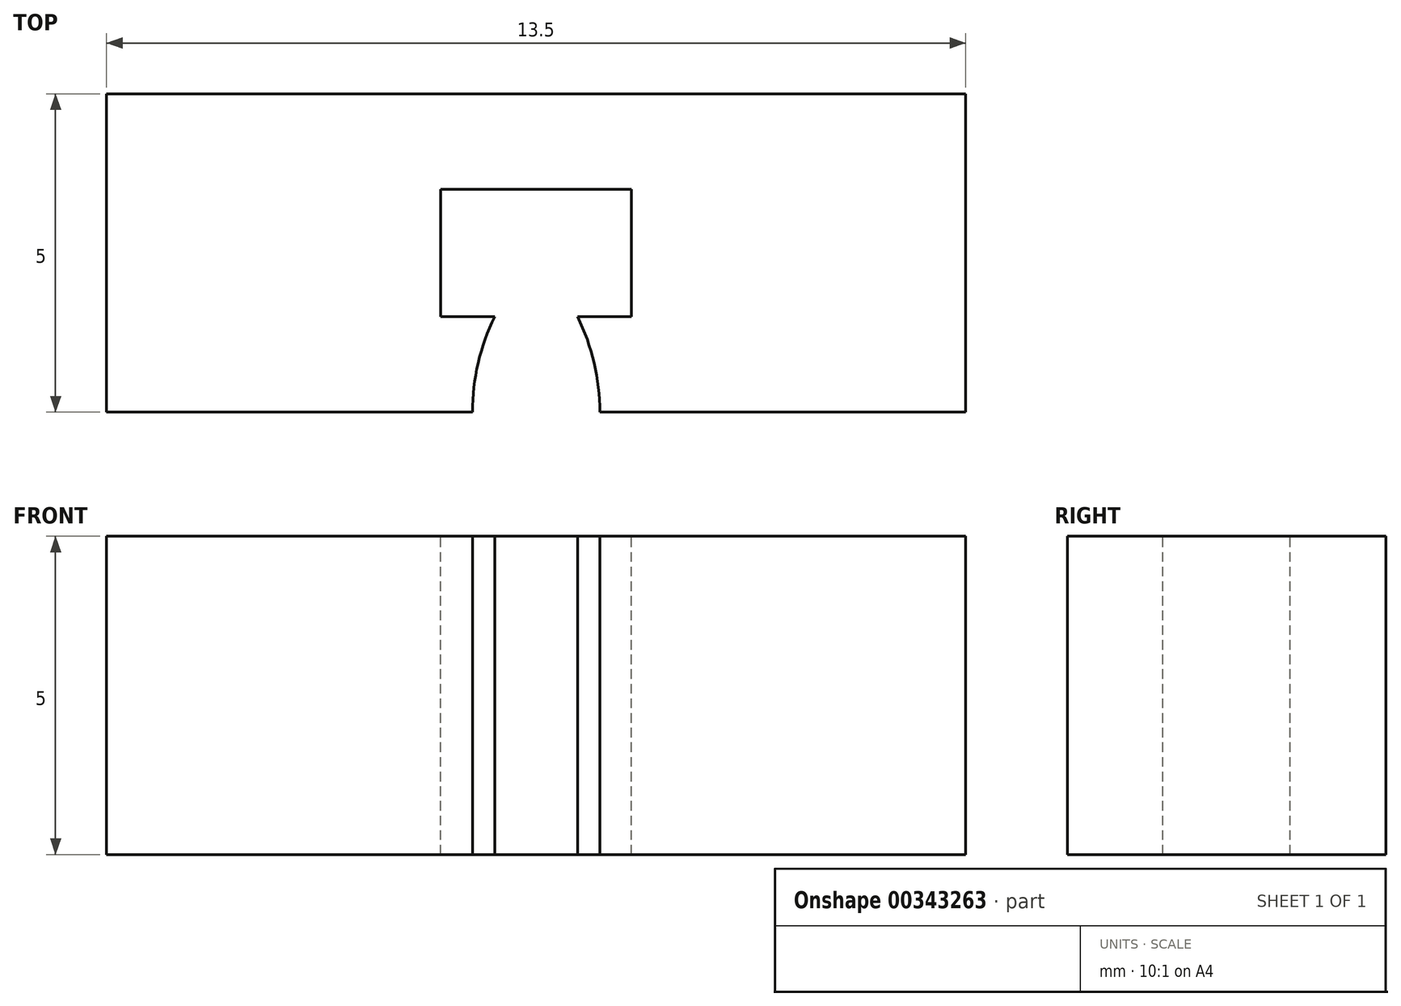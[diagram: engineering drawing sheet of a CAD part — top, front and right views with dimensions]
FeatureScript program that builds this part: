
annotation { "Feature Type Name" : "Feature", "Feature Type Description" : "" }
export const myFeature = defineFeature(function(context is Context, id is Id, definition is map)
    precondition{}
    {
        {
            var Q0;
            Q0=qCreatedBy(makeId("Top.planeOp"),FACE);
            var sketch = newSketch(context, id + "F0", { "sketchPlane" : qUnion([Q0])});
            skLineSegment(sketch, "E0.bottom", {"start": v(6.75, 2.5) * mm, "end": v(-6.75, 2.5) * mm});
            skLineSegment(sketch, "E0.top", {"start": v(6.75, -2.5) * mm, "end": v(-6.75, -2.5) * mm});
            skLineSegment(sketch, "E0.left", {"start": v(6.75, 2.5) * mm, "end": v(6.75, -2.5) * mm});
            skLineSegment(sketch, "E0.right", {"start": v(-6.75, 2.5) * mm, "end": v(-6.75, -2.5) * mm});
            skPoint(sketch, "E0.middle", {"position": v(0, 0) * mm});
            skSolve(sketch);
        }
        {
            var Q0;
            Q0=makeQuery(id+"F0.imprint","IMPRINT",FACE,{"disambiguationData":[TD([[makeQuery(id+"F0.imprint","IMPRINT",EDGE,{"derivedFrom":sQuery(id+"F0.wireOp",EDGE,"E0.bottom")}),1.0]])]});
            extrude(context, id + "F1", {"entities" : qUnion([Q0]), "depth" : 5 * mm});
        }
        {
            var Q0;
            Q0=makeQuery(id+"F1.opExtrude","CAP_FACE",FACE,{"disambiguationData":[OSD([sQuery(id+"F0.wireOp",EDGE,"E0.bottom"),sQuery(id+"F0.wireOp",EDGE,"E0.top"),sQuery(id+"F0.wireOp",EDGE,"E0.left"),sQuery(id+"F0.wireOp",EDGE,"E0.right")])],"isStart":false});
            var sketch = newSketch(context, id + "F2", { "sketchPlane" : qUnion([Q0])});
            skLineSegment(sketch, "E1.bottom", {"start": v(1.5, 1) * mm, "end": v(-1.5, 1) * mm});
            skLineSegment(sketch, "E1.top", {"start": v(1.5, -1) * mm, "end": v(-1.5, -1) * mm});
            skLineSegment(sketch, "E1.left", {"start": v(1.5, 1) * mm, "end": v(1.5, -1) * mm});
            skLineSegment(sketch, "E1.right", {"start": v(-1.5, 1) * mm, "end": v(-1.5, -1) * mm});
            skPoint(sketch, "E1.middle", {"position": v(0, 0) * mm});
            skLineSegment(sketch, "E2.bottom", {"start": v(1, -2.5) * mm, "end": v(-1, -2.5) * mm});
            skLineSegment(sketch, "E2.top", {"start": v(1, 0.5) * mm, "end": v(-1, 0.5) * mm});
            skLineSegment(sketch, "E2.left", {"start": v(1, -2.5) * mm, "end": v(1, 0.5) * mm});
            skLineSegment(sketch, "E2.right", {"start": v(-1, -2.5) * mm, "end": v(-1, 0.5) * mm});
            skPoint(sketch, "E2.middle", {"position": v(0, -1) * mm});
            skLineSegment(sketch, "E3", {"start": v(-1, -1) * mm, "end": v(-0.65, -1) * mm});
            skLineSegment(sketch, "E4", {"start": v(1, -1) * mm, "end": v(0.65, -1) * mm});
            skArc(sketch, "E5", {"start": v(-0.65, -1) * mm, "mid": v(-0.91, -1.73) * mm, "end": v(-1, -2.5) * mm});
            skArc(sketch, "E6", {"start": v(1, -2.5) * mm, "mid": v(0.91, -1.73) * mm, "end": v(0.65, -1) * mm});
            skSolve(sketch);
        }
        {
            var Q0;
            Q0=makeQuery(id+"F2.imprint","IMPRINT",FACE,{"disambiguationData":[TD([[makeQuery(id+"F2.imprint","IMPRINT",EDGE,{"derivedFrom":sQuery(id+"F2.wireOp",EDGE,"E1.bottom")}),1.0]])]});
            var Q1;
            {var subQ5=sQuery(id+"F2.wireOp",EDGE,"E2.top");Q1=makeQuery(id+"F2.imprint","IMPRINT",FACE,{"disambiguationData":[TD([[makeQuery(id+"F2.imprint","IMPRINT",EDGE,{"derivedFrom":subQ5}),1.0]])]});}
            var Q2;
            {var subQ5=sQuery(id+"F2.wireOp",EDGE,"E2.bottom");Q2=makeQuery(id+"F2.imprint","IMPRINT",FACE,{"disambiguationData":[TD([[makeQuery(id+"F2.imprint","IMPRINT",EDGE,{"derivedFrom":subQ5}),-1.0]])]});}
            extrude(context, id + "F3", {"entities" : qUnion([Q0, Q1, Q2]), "operationType" : NewBodyOperationType.REMOVE, "oppositeDirection" : true, "depth" : 25 * mm});
        }
    });
